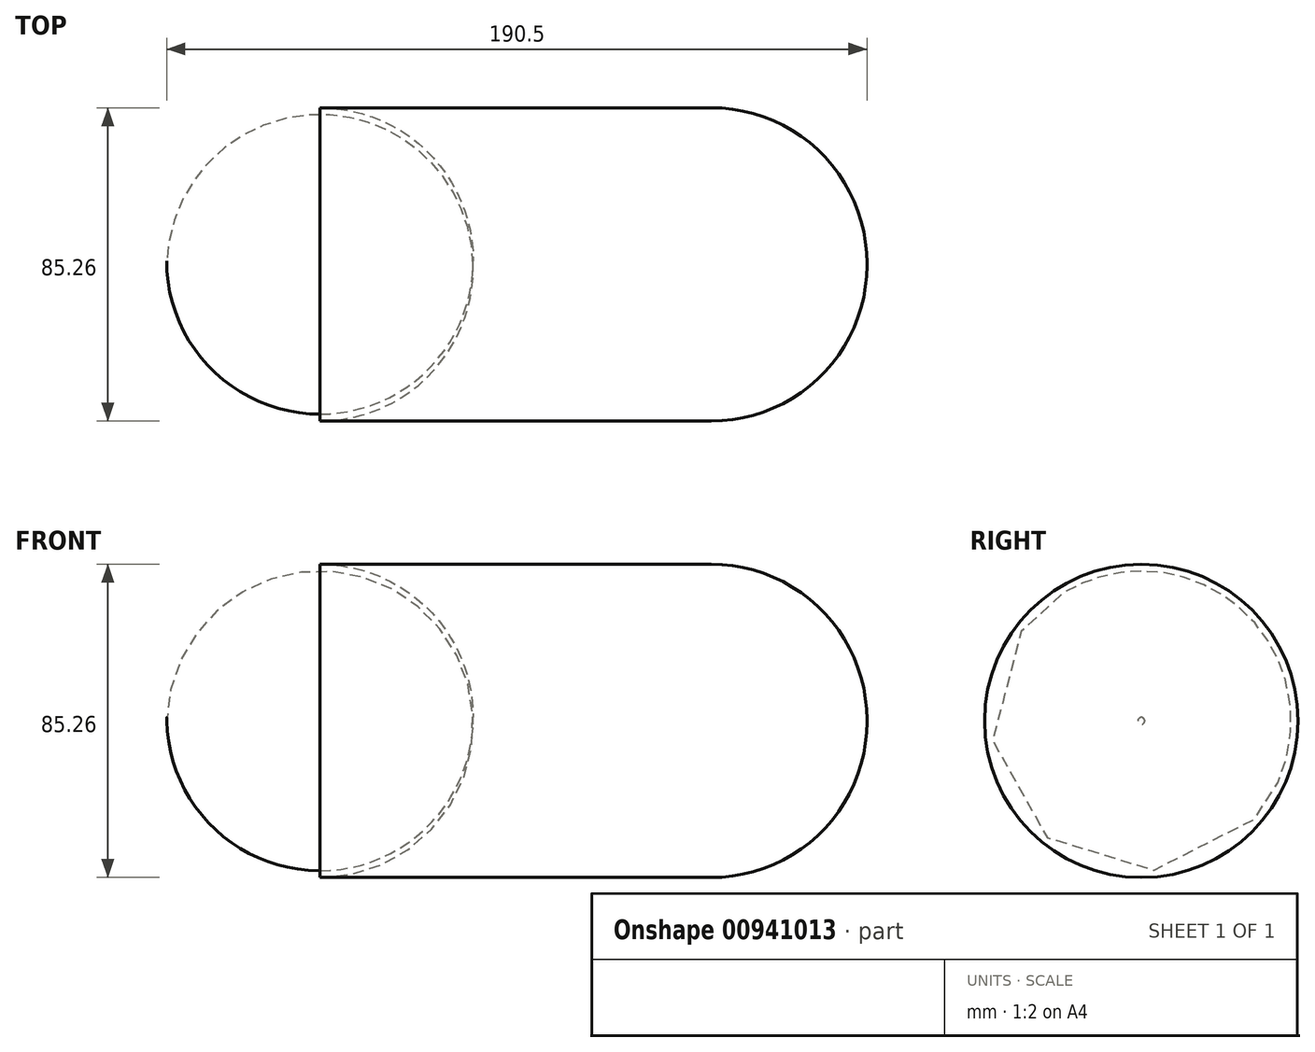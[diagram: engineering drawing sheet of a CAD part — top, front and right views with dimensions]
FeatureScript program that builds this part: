
annotation { "Feature Type Name" : "Feature", "Feature Type Description" : "" }
export const myFeature = defineFeature(function(context is Context, id is Id, definition is map)
    precondition{}
    {
        {
            var Q0;
            Q0=qCreatedBy(makeId("Right.planeOp"),FACE);
            var sketch = newSketch(context, id + "F0", { "sketchPlane" : qUnion([Q0])});
            skCircle(sketch, "E0", {"center": v(0, 0) * mm, "radius": 42.63 * mm});
            skSolve(sketch);
        }
        {
            var Q0;
            Q0 = qSketchRegion(id + "F0", true);
            extrude(context, id + "F1", {"entities" : qUnion([Q0]), "depth" : 190.5 * mm, "offsetDistance" : 25.4 * mm});
        }
        {
            var Q0;
            Q0=makeQuery(id+"F1.opExtrude","CAP_EDGE",EDGE,{"disambiguationData":[OSD([sQuery(id+"F0.wireOp",EDGE,"E0")])],"isStart":false});
            fillet(context, id + "F2", {"entities" : qUnion([Q0]), "radius" : 42.31 * mm, "tangentPropagation" : true, "allowEdgeOverflow" : false});
        }
        {
            var Q0;
            Q0=makeQuery(id+"F1.opExtrude","CAP_EDGE",EDGE,{"disambiguationData":[OSD([sQuery(id+"F0.wireOp",EDGE,"E0")])],"isStart":true});
            fillet(context, id + "F3", {"entities" : qUnion([Q0]), "radius" : 41.7 * mm, "tangentPropagation" : true, "allowEdgeOverflow" : false});
        }
    });
